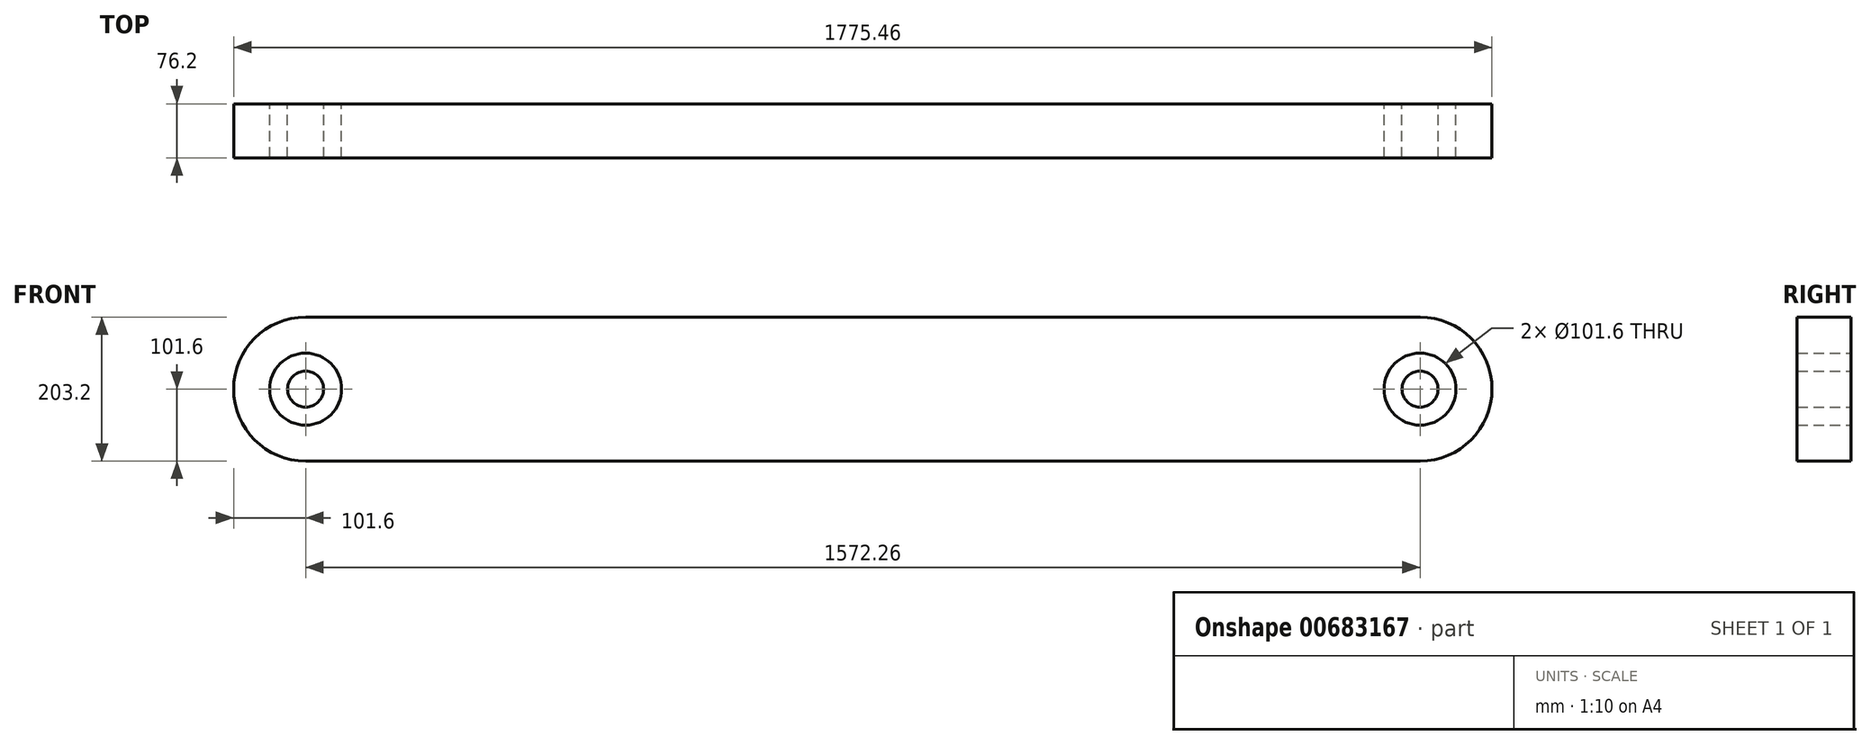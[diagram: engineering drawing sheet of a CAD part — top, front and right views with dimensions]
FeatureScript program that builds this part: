
annotation { "Feature Type Name" : "Feature", "Feature Type Description" : "" }
export const myFeature = defineFeature(function(context is Context, id is Id, definition is map)
    precondition{}
    {
        {
            var Q0;
            Q0=qCreatedBy(makeId("Front.planeOp"),FACE);
            var sketch = newSketch(context, id + "F0", { "sketchPlane" : qUnion([Q0])});
            skArc(sketch, "E0", {"start": v(0, 101.6) * mm, "mid": v(-101.6, 0) * mm, "end": v(0, -101.6) * mm});
            skArc(sketch, "E1", {"start": v(1572.26, -101.6) * mm, "mid": v(1673.86, 0) * mm, "end": v(1572.26, 101.6) * mm});
            skLineSegment(sketch, "E2", {"start": v(0, 101.6) * mm, "end": v(1572.26, 101.6) * mm});
            skLineSegment(sketch, "E3", {"start": v(0, -101.6) * mm, "end": v(1572.26, -101.6) * mm});
            skCircle(sketch, "E4", {"center": v(0, 0) * mm, "radius": 50.8 * mm});
            skCircle(sketch, "E5", {"center": v(1572.26, 0) * mm, "radius": 50.8 * mm});
            skCircle(sketch, "E6", {"center": v(0, 0) * mm, "radius": 25.4 * mm});
            skCircle(sketch, "E7", {"center": v(1572.26, 0) * mm, "radius": 25.4 * mm});
            skSolve(sketch);
        }
        {
            var Q0;
            Q0=makeQuery(id+"F0.imprint","IMPRINT",FACE,{"disambiguationData":[TD([[makeQuery(id+"F0.imprint","IMPRINT",EDGE,{"derivedFrom":sQuery(id+"F0.wireOp",EDGE,"E0")}),1.0]])]});
            var Q1;
            Q1=makeQuery(id+"F0.imprint","IMPRINT",FACE,{"disambiguationData":[TD([[makeQuery(id+"F0.imprint","IMPRINT",EDGE,{"derivedFrom":sQuery(id+"F0.wireOp",EDGE,"E6")}),1.0]])]});
            var Q2;
            Q2=makeQuery(id+"F0.imprint","IMPRINT",FACE,{"disambiguationData":[TD([[makeQuery(id+"F0.imprint","IMPRINT",EDGE,{"derivedFrom":sQuery(id+"F0.wireOp",EDGE,"E7")}),1.0]])]});
            extrude(context, id + "F1", {"entities" : qUnion([Q0, Q1, Q2]), "depth" : 76.2 * mm, "offsetDistance" : 25.4 * mm});
        }
    });
